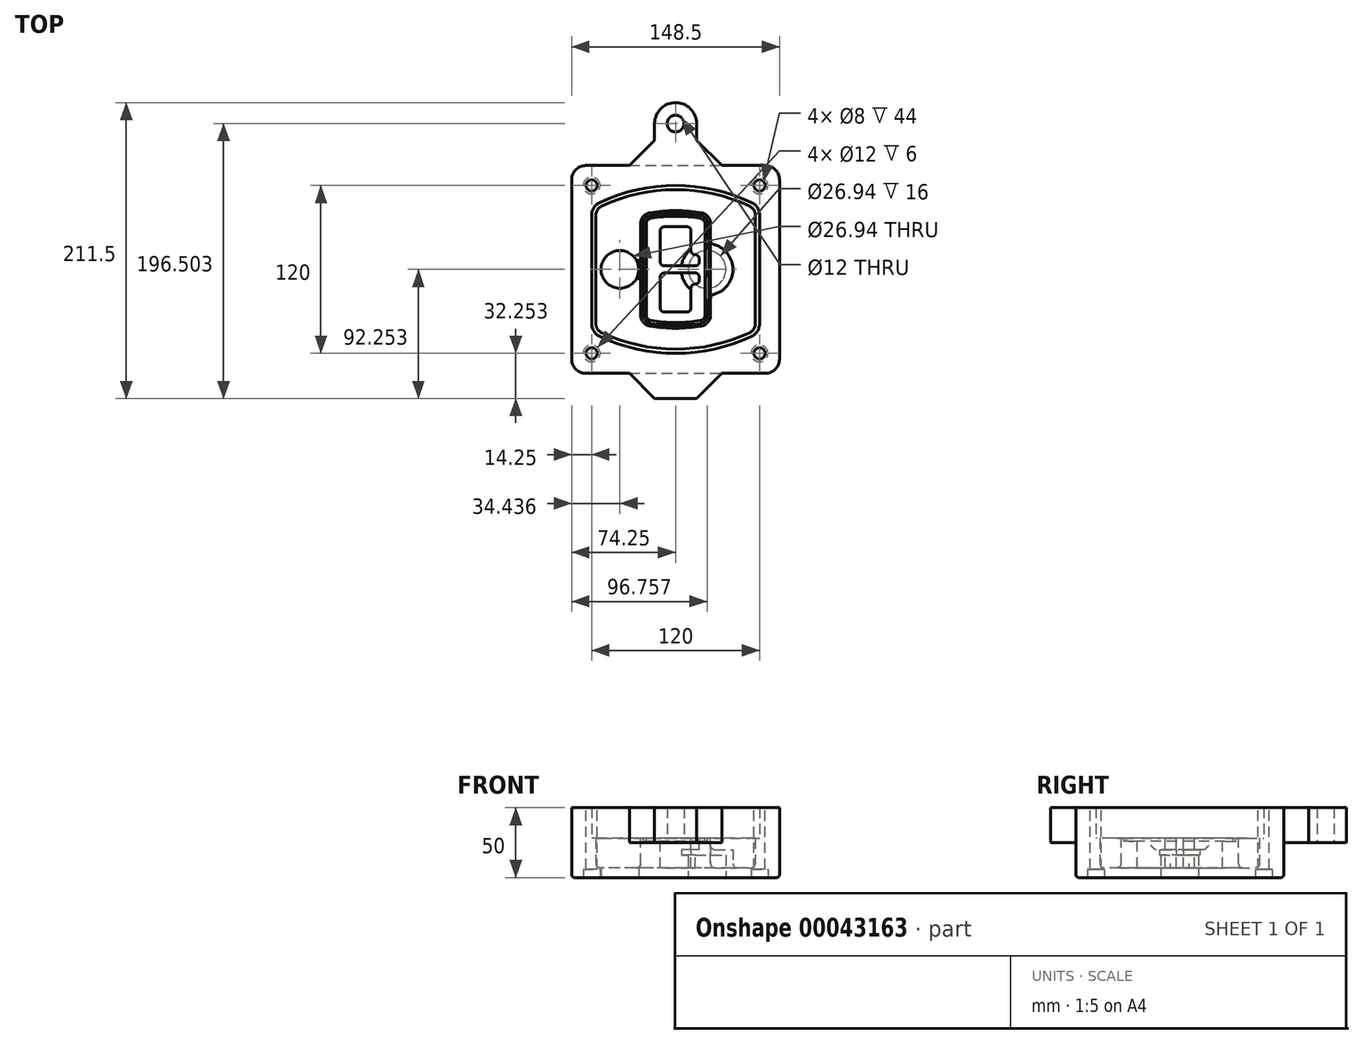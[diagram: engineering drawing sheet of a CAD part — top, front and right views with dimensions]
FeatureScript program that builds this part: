
annotation { "Feature Type Name" : "Feature", "Feature Type Description" : "" }
export const myFeature = defineFeature(function(context is Context, id is Id, definition is map)
    precondition{}
    {
        {
            var Q0;
            Q0=qCreatedBy(makeId("Top.planeOp"),FACE);
            var sketch = newSketch(context, id + "F0", { "sketchPlane" : qUnion([Q0])});
            skPoint(sketch, "E0.rect.middle", {"position": v(0, 0) * mm});
            skLineSegment(sketch, "E1.bottom", {"start": v(24.05, 28.38) * mm, "end": v(152.55, 28.38) * mm});
            skLineSegment(sketch, "E1.top", {"start": v(24.05, 176.88) * mm, "end": v(152.55, 176.88) * mm});
            skLineSegment(sketch, "E1.left", {"start": v(14.05, 38.38) * mm, "end": v(14.05, 166.88) * mm});
            skLineSegment(sketch, "E1.right", {"start": v(162.55, 38.38) * mm, "end": v(162.55, 166.88) * mm});
            skLineSegment(sketch, "E2", {"start": v(14.05, 176.88) * mm, "end": v(162.55, 28.38) * mm, "construction": true});
            skLineSegment(sketch, "E3", {"start": v(162.55, 176.88) * mm, "end": v(14.05, 28.38) * mm, "construction": true});
            skCircle(sketch, "E4", {"center": v(28.3, 162.63) * mm, "radius": 4 * mm});
            skCircle(sketch, "E5", {"center": v(148.3, 162.63) * mm, "radius": 4 * mm});
            skCircle(sketch, "E6", {"center": v(148.3, 42.63) * mm, "radius": 4 * mm});
            skCircle(sketch, "E7", {"center": v(28.3, 42.63) * mm, "radius": 4 * mm});
            skLineSegment(sketch, "E8", {"start": v(28.3, 162.63) * mm, "end": v(148.3, 162.63) * mm, "construction": true});
            skLineSegment(sketch, "E9", {"start": v(148.3, 162.63) * mm, "end": v(148.3, 42.63) * mm, "construction": true});
            skLineSegment(sketch, "E10", {"start": v(148.3, 42.63) * mm, "end": v(28.3, 42.63) * mm, "construction": true});
            skLineSegment(sketch, "E11", {"start": v(28.3, 42.63) * mm, "end": v(28.3, 162.63) * mm, "construction": true});
            skLineSegment(sketch, "E12", {"start": v(28.3, 141.46) * mm, "end": v(28.3, 63.8) * mm});
            skLineSegment(sketch, "E13", {"start": v(148.3, 141.46) * mm, "end": v(148.3, 63.8) * mm});
            skArc(sketch, "E14", {"start": v(142.56, 150.51) * mm, "mid": v(88.3, 162.63) * mm, "end": v(34.04, 150.51) * mm});
            skArc(sketch, "E15", {"start": v(34.04, 54.75) * mm, "mid": v(88.3, 42.63) * mm, "end": v(142.56, 54.75) * mm});
            skLineSegment(sketch, "E16", {"start": v(28.3, 102.63) * mm, "end": v(148.3, 102.63) * mm, "construction": true});
            skPoint(sketch, "E17.visualSharp", {"position": v(28.3, 57.63) * mm});
            skArc(sketch, "E17.filletArc", {"start": v(28.3, 63.8) * mm, "mid": v(29.86, 58.44) * mm, "end": v(34.04, 54.75) * mm});
            skPoint(sketch, "E18.visualSharp", {"position": v(28.3, 147.63) * mm});
            skArc(sketch, "E18.filletArc", {"start": v(34.04, 150.51) * mm, "mid": v(29.86, 146.82) * mm, "end": v(28.3, 141.46) * mm});
            skPoint(sketch, "E19.visualSharp", {"position": v(148.3, 147.63) * mm});
            skArc(sketch, "E19.filletArc", {"start": v(148.3, 141.46) * mm, "mid": v(146.74, 146.82) * mm, "end": v(142.56, 150.51) * mm});
            skPoint(sketch, "E20.visualSharp", {"position": v(148.3, 57.63) * mm});
            skArc(sketch, "E20.filletArc", {"start": v(142.56, 54.75) * mm, "mid": v(146.74, 58.44) * mm, "end": v(148.3, 63.8) * mm});
            skPoint(sketch, "E21.visualSharp", {"position": v(14.05, 176.88) * mm});
            skArc(sketch, "E21.filletArc", {"start": v(24.05, 176.88) * mm, "mid": v(16.98, 173.95) * mm, "end": v(14.05, 166.88) * mm});
            skPoint(sketch, "E22.visualSharp", {"position": v(162.55, 176.88) * mm});
            skArc(sketch, "E22.filletArc", {"start": v(162.55, 166.88) * mm, "mid": v(159.62, 173.95) * mm, "end": v(152.55, 176.88) * mm});
            skPoint(sketch, "E23.visualSharp", {"position": v(162.55, 28.38) * mm});
            skArc(sketch, "E23.filletArc", {"start": v(152.55, 28.38) * mm, "mid": v(159.62, 31.31) * mm, "end": v(162.55, 38.38) * mm});
            skPoint(sketch, "E24.visualSharp", {"position": v(14.05, 28.38) * mm});
            skArc(sketch, "E24.filletArc", {"start": v(14.05, 38.38) * mm, "mid": v(16.98, 31.31) * mm, "end": v(24.05, 28.38) * mm});
            skArc(sketch, "E25.0", {"start": v(145.3, 141.46) * mm, "mid": v(144.2, 145.22) * mm, "end": v(141.28, 147.8) * mm});
            skLineSegment(sketch, "E25.1", {"start": v(145.3, 141.46) * mm, "end": v(145.3, 63.8) * mm});
            skArc(sketch, "E25.2", {"start": v(141.28, 57.47) * mm, "mid": v(144.2, 60.05) * mm, "end": v(145.3, 63.8) * mm});
            skArc(sketch, "E25.3", {"start": v(35.32, 57.47) * mm, "mid": v(88.3, 45.63) * mm, "end": v(141.28, 57.47) * mm});
            skArc(sketch, "E25.4", {"start": v(31.3, 63.8) * mm, "mid": v(32.4, 60.05) * mm, "end": v(35.32, 57.47) * mm});
            skArc(sketch, "E25.5", {"start": v(141.28, 147.8) * mm, "mid": v(88.3, 159.63) * mm, "end": v(35.32, 147.8) * mm});
            skLineSegment(sketch, "E25.6", {"start": v(31.3, 141.46) * mm, "end": v(31.3, 63.8) * mm});
            skArc(sketch, "E25.7", {"start": v(35.32, 147.8) * mm, "mid": v(32.4, 145.22) * mm, "end": v(31.3, 141.46) * mm});
            skArc(sketch, "E26.0", {"start": v(32.34, 154.13) * mm, "mid": v(26.48, 148.97) * mm, "end": v(24.3, 141.46) * mm});
            skArc(sketch, "E26.1", {"start": v(144.26, 154.13) * mm, "mid": v(88.3, 166.63) * mm, "end": v(32.34, 154.13) * mm});
            skArc(sketch, "E26.2", {"start": v(152.3, 141.46) * mm, "mid": v(150.12, 148.97) * mm, "end": v(144.26, 154.13) * mm});
            skLineSegment(sketch, "E26.3", {"start": v(152.3, 141.46) * mm, "end": v(152.3, 63.8) * mm});
            skArc(sketch, "E26.4", {"start": v(144.26, 51.13) * mm, "mid": v(150.12, 56.3) * mm, "end": v(152.3, 63.8) * mm});
            skLineSegment(sketch, "E26.5", {"start": v(24.3, 141.46) * mm, "end": v(24.3, 63.8) * mm});
            skArc(sketch, "E26.6", {"start": v(32.34, 51.13) * mm, "mid": v(88.3, 38.63) * mm, "end": v(144.26, 51.13) * mm});
            skArc(sketch, "E26.7", {"start": v(24.3, 63.8) * mm, "mid": v(26.48, 56.3) * mm, "end": v(32.34, 51.13) * mm});
            skSolve(sketch);
        }
        {
            var Q0;
            Q0=makeQuery(id+"F0.imprint","IMPRINT",FACE,{"disambiguationData":[TD([[makeQuery(id+"F0.imprint","IMPRINT",EDGE,{"derivedFrom":sQuery(id+"F0.wireOp",EDGE,"E1.bottom")}),1.0]])]});
            var Q1;
            Q1=makeQuery(id+"F0.imprint","IMPRINT",FACE,{"disambiguationData":[TD([[makeQuery(id+"F0.imprint","IMPRINT",EDGE,{"derivedFrom":sQuery(id+"F0.wireOp",EDGE,"E12")}),1.0]])]});
            var Q2;
            Q2=makeQuery(id+"F0.imprint","IMPRINT",FACE,{"disambiguationData":[TD([[makeQuery(id+"F0.imprint","IMPRINT",EDGE,{"derivedFrom":sQuery(id+"F0.wireOp",EDGE,"E25.0")}),1.0]])]});
            var Q3;
            Q3=makeQuery(id+"F0.imprint","IMPRINT",FACE,{"disambiguationData":[TD([[makeQuery(id+"F0.imprint","IMPRINT",EDGE,{"derivedFrom":sQuery(id+"F0.wireOp",EDGE,"E12")}),-1.0]])]});
            extrude(context, id + "F1", {"entities" : qUnion([Q0, Q1, Q2, Q3]), "oppositeDirection" : true, "depth" : 25 * mm});
        }
        {
            var Q0;
            Q0=makeQuery(id+"F0.imprint","IMPRINT",FACE,{"disambiguationData":[TD([[makeQuery(id+"F0.imprint","IMPRINT",EDGE,{"derivedFrom":sQuery(id+"F0.wireOp",EDGE,"E12")}),1.0]])]});
            extrude(context, id + "F2", {"entities" : qUnion([Q0]), "operationType" : NewBodyOperationType.ADD, "depth" : 3 * mm});
        }
        {
            var Q0;
            Q0=makeQuery(id+"F0.imprint","IMPRINT",FACE,{"disambiguationData":[TD([[makeQuery(id+"F0.imprint","IMPRINT",EDGE,{"derivedFrom":sQuery(id+"F0.wireOp",EDGE,"E25.0")}),1.0]])]});
            extrude(context, id + "F3", {"entities" : qUnion([Q0]), "operationType" : NewBodyOperationType.REMOVE, "oppositeDirection" : true, "depth" : 18 * mm});
        }
        {
            var Q0;
            Q0=makeQuery(id+"F2.opExtrude","CAP_FACE",FACE,{"disambiguationData":[OSD([sQuery(id+"F0.wireOp",EDGE,"E12"),sQuery(id+"F0.wireOp",EDGE,"E13"),sQuery(id+"F0.wireOp",EDGE,"E14"),sQuery(id+"F0.wireOp",EDGE,"E15"),sQuery(id+"F0.wireOp",EDGE,"E17.filletArc"),sQuery(id+"F0.wireOp",EDGE,"E18.filletArc"),sQuery(id+"F0.wireOp",EDGE,"E19.filletArc"),sQuery(id+"F0.wireOp",EDGE,"E20.filletArc"),sQuery(id+"F0.wireOp",EDGE,"E25.0"),sQuery(id+"F0.wireOp",EDGE,"E25.1"),sQuery(id+"F0.wireOp",EDGE,"E25.2"),sQuery(id+"F0.wireOp",EDGE,"E25.3"),sQuery(id+"F0.wireOp",EDGE,"E25.4"),sQuery(id+"F0.wireOp",EDGE,"E25.5"),sQuery(id+"F0.wireOp",EDGE,"E25.6"),sQuery(id+"F0.wireOp",EDGE,"E25.7")])],"isStart":false});
            var sketch = newSketch(context, id + "F4", { "sketchPlane" : qUnion([Q0])});
            skArc(sketch, "E27.0", {"start": v(69.96, 62.18) * mm, "mid": v(88.3, 60.63) * mm, "end": v(106.64, 62.18) * mm});
            skArc(sketch, "E28.0", {"start": v(106.64, 143.09) * mm, "mid": v(88.3, 144.63) * mm, "end": v(69.96, 143.09) * mm});
            skLineSegment(sketch, "E29", {"start": v(63.3, 135.2) * mm, "end": v(63.3, 70.07) * mm});
            skLineSegment(sketch, "E30", {"start": v(113.3, 135.2) * mm, "end": v(113.3, 70.07) * mm});
            skLineSegment(sketch, "E31", {"start": v(63.3, 141.74) * mm, "end": v(113.3, 141.74) * mm, "construction": true});
            skLineSegment(sketch, "E32", {"start": v(63.3, 63.52) * mm, "end": v(113.3, 63.52) * mm, "construction": true});
            skPoint(sketch, "E33.visualSharp", {"position": v(63.3, 141.74) * mm});
            skArc(sketch, "E33.filletArc", {"start": v(69.96, 143.09) * mm, "mid": v(65.19, 140.36) * mm, "end": v(63.3, 135.2) * mm});
            skPoint(sketch, "E34.visualSharp", {"position": v(113.3, 141.74) * mm});
            skArc(sketch, "E34.filletArc", {"start": v(113.3, 135.2) * mm, "mid": v(111.41, 140.36) * mm, "end": v(106.64, 143.09) * mm});
            skPoint(sketch, "E35.visualSharp", {"position": v(113.3, 63.52) * mm});
            skArc(sketch, "E35.filletArc", {"start": v(106.64, 62.18) * mm, "mid": v(111.41, 64.9) * mm, "end": v(113.3, 70.07) * mm});
            skPoint(sketch, "E36.visualSharp", {"position": v(63.3, 63.52) * mm});
            skArc(sketch, "E36.filletArc", {"start": v(63.3, 70.07) * mm, "mid": v(65.19, 64.9) * mm, "end": v(69.96, 62.18) * mm});
            skArc(sketch, "E37.0", {"start": v(141.28, 147.8) * mm, "mid": v(88.3, 159.63) * mm, "end": v(35.32, 147.8) * mm});
            skArc(sketch, "E37.1", {"start": v(35.32, 147.8) * mm, "mid": v(32.4, 145.22) * mm, "end": v(31.3, 141.46) * mm});
            skLineSegment(sketch, "E37.2", {"start": v(31.3, 141.46) * mm, "end": v(31.3, 63.8) * mm});
            skArc(sketch, "E37.3", {"start": v(31.3, 63.8) * mm, "mid": v(32.4, 60.05) * mm, "end": v(35.32, 57.47) * mm});
            skArc(sketch, "E37.4", {"start": v(35.32, 57.47) * mm, "mid": v(88.3, 45.63) * mm, "end": v(141.28, 57.47) * mm});
            skArc(sketch, "E37.5", {"start": v(141.28, 57.47) * mm, "mid": v(144.2, 60.05) * mm, "end": v(145.3, 63.8) * mm});
            skLineSegment(sketch, "E37.6", {"start": v(145.3, 141.46) * mm, "end": v(145.3, 63.8) * mm});
            skArc(sketch, "E37.7", {"start": v(145.3, 141.46) * mm, "mid": v(144.2, 145.22) * mm, "end": v(141.28, 147.8) * mm});
            skLineSegment(sketch, "E38.0", {"start": v(111.3, 135.2) * mm, "end": v(111.3, 70.07) * mm});
            skArc(sketch, "E38.1", {"start": v(106.3, 64.15) * mm, "mid": v(109.88, 66.2) * mm, "end": v(111.3, 70.07) * mm});
            skArc(sketch, "E38.2", {"start": v(70.3, 64.15) * mm, "mid": v(88.3, 62.63) * mm, "end": v(106.3, 64.15) * mm});
            skArc(sketch, "E38.3", {"start": v(65.3, 70.07) * mm, "mid": v(66.72, 66.2) * mm, "end": v(70.3, 64.15) * mm});
            skLineSegment(sketch, "E38.4", {"start": v(65.3, 135.2) * mm, "end": v(65.3, 70.07) * mm});
            skArc(sketch, "E38.5", {"start": v(111.3, 135.2) * mm, "mid": v(109.88, 139.07) * mm, "end": v(106.3, 141.11) * mm});
            skArc(sketch, "E38.6", {"start": v(70.3, 141.11) * mm, "mid": v(66.72, 139.07) * mm, "end": v(65.3, 135.2) * mm});
            skArc(sketch, "E38.7", {"start": v(106.3, 141.11) * mm, "mid": v(88.3, 142.63) * mm, "end": v(70.3, 141.11) * mm});
            skArc(sketch, "E39.0", {"start": v(109.3, 135.2) * mm, "mid": v(108.36, 137.78) * mm, "end": v(105.97, 139.14) * mm});
            skLineSegment(sketch, "E39.1", {"start": v(109.3, 135.2) * mm, "end": v(109.3, 70.07) * mm});
            skArc(sketch, "E39.2", {"start": v(105.97, 66.12) * mm, "mid": v(108.36, 67.49) * mm, "end": v(109.3, 70.07) * mm});
            skArc(sketch, "E39.3", {"start": v(70.63, 66.12) * mm, "mid": v(88.3, 64.63) * mm, "end": v(105.97, 66.12) * mm});
            skArc(sketch, "E39.4", {"start": v(67.3, 70.07) * mm, "mid": v(68.24, 67.49) * mm, "end": v(70.63, 66.12) * mm});
            skArc(sketch, "E39.5", {"start": v(105.97, 139.14) * mm, "mid": v(88.3, 140.63) * mm, "end": v(70.63, 139.14) * mm});
            skLineSegment(sketch, "E39.6", {"start": v(67.3, 135.2) * mm, "end": v(67.3, 70.07) * mm});
            skArc(sketch, "E39.7", {"start": v(70.63, 139.14) * mm, "mid": v(68.24, 137.78) * mm, "end": v(67.3, 135.2) * mm});
            skLineSegment(sketch, "E40", {"start": v(63.3, 102.63) * mm, "end": v(113.3, 102.63) * mm, "construction": true});
            skLineSegment(sketch, "E41", {"start": v(77.3, 108.13) * mm, "end": v(77.3, 130.13) * mm});
            skLineSegment(sketch, "E42", {"start": v(80.3, 133.13) * mm, "end": v(96.3, 133.13) * mm});
            skLineSegment(sketch, "E43", {"start": v(99.3, 130.13) * mm, "end": v(99.3, 116.13) * mm});
            skLineSegment(sketch, "E44", {"start": v(102.3, 113.13) * mm, "end": v(102.3, 113.13) * mm});
            skLineSegment(sketch, "E45", {"start": v(105.3, 110.13) * mm, "end": v(105.3, 108.13) * mm});
            skLineSegment(sketch, "E46", {"start": v(102.3, 105.13) * mm, "end": v(80.3, 105.13) * mm});
            skPoint(sketch, "E47.visualSharp", {"position": v(77.3, 133.13) * mm});
            skArc(sketch, "E47.filletArc", {"start": v(80.3, 133.13) * mm, "mid": v(78.18, 132.25) * mm, "end": v(77.3, 130.13) * mm});
            skPoint(sketch, "E48.visualSharp", {"position": v(99.3, 133.13) * mm});
            skArc(sketch, "E48.filletArc", {"start": v(99.3, 130.13) * mm, "mid": v(98.42, 132.25) * mm, "end": v(96.3, 133.13) * mm});
            skPoint(sketch, "E49.visualSharp", {"position": v(99.3, 113.13) * mm});
            skArc(sketch, "E49.filletArc", {"start": v(99.3, 116.13) * mm, "mid": v(100.18, 114.01) * mm, "end": v(102.3, 113.13) * mm});
            skPoint(sketch, "E50.visualSharp", {"position": v(105.3, 113.13) * mm});
            skArc(sketch, "E50.filletArc", {"start": v(105.3, 110.13) * mm, "mid": v(104.42, 112.25) * mm, "end": v(102.3, 113.13) * mm});
            skPoint(sketch, "E51.visualSharp", {"position": v(105.3, 105.13) * mm});
            skArc(sketch, "E51.filletArc", {"start": v(102.3, 105.13) * mm, "mid": v(104.42, 106.01) * mm, "end": v(105.3, 108.13) * mm});
            skPoint(sketch, "E52.visualSharp", {"position": v(77.3, 105.13) * mm});
            skArc(sketch, "E52.filletArc", {"start": v(77.3, 108.13) * mm, "mid": v(78.18, 106.01) * mm, "end": v(80.3, 105.13) * mm});
            skLineSegment(sketch, "E53.0.MirrorCS", {"start": v(102.3, 100.13) * mm, "end": v(80.3, 100.13) * mm});
            skArc(sketch, "E54.0.MirrorCS", {"start": v(77.3, 97.13) * mm, "mid": v(78.18, 99.25) * mm, "end": v(80.3, 100.13) * mm});
            skLineSegment(sketch, "E55.0.MirrorCS", {"start": v(77.3, 97.13) * mm, "end": v(77.3, 75.13) * mm});
            skArc(sketch, "E56.0.MirrorCS", {"start": v(80.3, 72.13) * mm, "mid": v(78.18, 73.01) * mm, "end": v(77.3, 75.13) * mm});
            skLineSegment(sketch, "E57.0.MirrorCS", {"start": v(80.3, 72.13) * mm, "end": v(96.3, 72.13) * mm});
            skArc(sketch, "E58.0.MirrorCS", {"start": v(99.3, 75.13) * mm, "mid": v(98.42, 73.01) * mm, "end": v(96.3, 72.13) * mm});
            skLineSegment(sketch, "E59.0.MirrorCS", {"start": v(99.3, 75.13) * mm, "end": v(99.3, 89.13) * mm});
            skArc(sketch, "E60.0.MirrorCS", {"start": v(99.3, 89.13) * mm, "mid": v(100.18, 91.25) * mm, "end": v(102.3, 92.13) * mm});
            skArc(sketch, "E61.0.MirrorCS", {"start": v(105.3, 95.13) * mm, "mid": v(104.42, 93.01) * mm, "end": v(102.3, 92.13) * mm});
            skLineSegment(sketch, "E62.0.MirrorCS", {"start": v(105.3, 95.13) * mm, "end": v(105.3, 97.13) * mm});
            skArc(sketch, "E63.0.MirrorCS", {"start": v(102.3, 100.13) * mm, "mid": v(104.42, 99.25) * mm, "end": v(105.3, 97.13) * mm});
            skSolve(sketch);
        }
        {
            var Q0;
            Q0=makeQuery(id+"F4.imprint","IMPRINT",FACE,{"disambiguationData":[TD([[makeQuery(id+"F4.imprint","IMPRINT",EDGE,{"derivedFrom":sQuery(id+"F4.wireOp",EDGE,"E27.0")}),1.0]])]});
            var Q1;
            Q1=makeQuery(id+"F4.imprint","IMPRINT",FACE,{"disambiguationData":[TD([[makeQuery(id+"F4.imprint","IMPRINT",EDGE,{"derivedFrom":sQuery(id+"F4.wireOp",EDGE,"E38.0")}),-1.0]])]});
            var Q2;
            Q2=makeQuery(id+"F4.imprint","IMPRINT",FACE,{"disambiguationData":[TD([[makeQuery(id+"F4.imprint","IMPRINT",EDGE,{"derivedFrom":sQuery(id+"F4.wireOp",EDGE,"E39.0")}),1.0]])]});
            extrude(context, id + "F5", {"entities" : qUnion([Q0, Q1, Q2]), "operationType" : NewBodyOperationType.ADD, "endBound" : BoundingType.UP_TO_NEXT, "oppositeDirection" : true, "depth" : 25 * mm});
        }
        {
            var Q0;
            Q0=makeQuery(id+"F4.imprint","IMPRINT",FACE,{"disambiguationData":[TD([[makeQuery(id+"F4.imprint","IMPRINT",EDGE,{"derivedFrom":sQuery(id+"F4.wireOp",EDGE,"E38.0")}),-1.0]])]});
            extrude(context, id + "F6", {"entities" : qUnion([Q0]), "operationType" : NewBodyOperationType.REMOVE, "oppositeDirection" : true, "depth" : 2 * mm});
        }
        {
            var Q0;
            Q0=makeQuery(id+"F1.opExtrude","CAP_FACE",FACE,{"disambiguationData":[OSD([sQuery(id+"F0.wireOp",EDGE,"E1.bottom"),sQuery(id+"F0.wireOp",EDGE,"E1.top"),sQuery(id+"F0.wireOp",EDGE,"E1.left"),sQuery(id+"F0.wireOp",EDGE,"E1.right"),sQuery(id+"F0.wireOp",EDGE,"E4"),sQuery(id+"F0.wireOp",EDGE,"E5"),sQuery(id+"F0.wireOp",EDGE,"E6"),sQuery(id+"F0.wireOp",EDGE,"E7"),sQuery(id+"F0.wireOp",EDGE,"E21.filletArc"),sQuery(id+"F0.wireOp",EDGE,"E22.filletArc"),sQuery(id+"F0.wireOp",EDGE,"E23.filletArc"),sQuery(id+"F0.wireOp",EDGE,"E24.filletArc")])],"isStart":false});
            var sketch = newSketch(context, id + "F7", { "sketchPlane" : qUnion([Q0])});
            skCircle(sketch, "E64", {"center": v(110.8, -102.63) * mm, "radius": 13.47 * mm});
            skCircle(sketch, "E65", {"center": v(48.49, -102.63) * mm, "radius": 13.47 * mm});
            skLineSegment(sketch, "E66", {"start": v(162.55, -102.63) * mm, "end": v(14.05, -102.63) * mm});
            skCircle(sketch, "E67", {"center": v(110.8, -102.63) * mm, "radius": 18.47 * mm});
            skCircle(sketch, "E68", {"center": v(148.3, -162.63) * mm, "radius": 6 * mm});
            skCircle(sketch, "E69", {"center": v(28.3, -162.63) * mm, "radius": 6 * mm});
            skCircle(sketch, "E70", {"center": v(28.3, -42.63) * mm, "radius": 6 * mm});
            skCircle(sketch, "E71", {"center": v(148.3, -42.63) * mm, "radius": 6 * mm});
            skSolve(sketch);
        }
        {
            var Q0;
            {var subQ1=sQuery(id+"F7.wireOp",EDGE,"E66");var subQ4=sQuery(id+"F7.wireOp",EDGE,"E64");var subQ6=makeQuery(id+"F7.imprint","INTERSECT",VERTEX,{"disambiguationData":[OD(0.0)],"derivedFrom":[subQ4,subQ1]});Q0=makeQuery(id+"F7.imprint","IMPRINT",FACE,{"disambiguationData":[TD([[makeQuery(id+"F7.imprint","IMPRINT",EDGE,{"disambiguationData":[TD([[subQ6,-1.0]])],"derivedFrom":subQ4}),-1.0]])]});}
            var Q1;
            {var subQ0=sQuery(id+"F7.wireOp",EDGE,"E66");var subQ1=sQuery(id+"F7.wireOp",EDGE,"E64");var subQ3=makeQuery(id+"F7.imprint","INTERSECT",VERTEX,{"disambiguationData":[OD(0.0)],"derivedFrom":[subQ1,subQ0]});Q1=makeQuery(id+"F7.imprint","IMPRINT",FACE,{"disambiguationData":[TD([[makeQuery(id+"F7.imprint","IMPRINT",EDGE,{"disambiguationData":[TD([[subQ3,-1.0]])],"derivedFrom":subQ1}),1.0]])]});}
            var Q2;
            {var subQ0=sQuery(id+"F7.wireOp",EDGE,"E66");var subQ1=sQuery(id+"F7.wireOp",EDGE,"E64");var subQ3=makeQuery(id+"F7.imprint","INTERSECT",VERTEX,{"disambiguationData":[OD(0.0)],"derivedFrom":[subQ1,subQ0]});Q2=makeQuery(id+"F7.imprint","IMPRINT",FACE,{"disambiguationData":[TD([[makeQuery(id+"F7.imprint","IMPRINT",EDGE,{"disambiguationData":[TD([[subQ3,1.0]])],"derivedFrom":subQ1}),1.0]])]});}
            var Q3;
            {var subQ1=sQuery(id+"F7.wireOp",EDGE,"E66");var subQ4=sQuery(id+"F7.wireOp",EDGE,"E64");var subQ6=makeQuery(id+"F7.imprint","INTERSECT",VERTEX,{"disambiguationData":[OD(0.0)],"derivedFrom":[subQ4,subQ1]});Q3=makeQuery(id+"F7.imprint","IMPRINT",FACE,{"disambiguationData":[TD([[makeQuery(id+"F7.imprint","IMPRINT",EDGE,{"disambiguationData":[TD([[subQ6,1.0]])],"derivedFrom":subQ4}),-1.0]])]});}
            extrude(context, id + "F8", {"entities" : qUnion([Q0, Q1, Q2, Q3]), "operationType" : NewBodyOperationType.ADD, "oppositeDirection" : true, "depth" : 20 * mm});
        }
        {
            var Q0;
            {var subQ0=sQuery(id+"F7.wireOp",EDGE,"E66");var subQ1=sQuery(id+"F7.wireOp",EDGE,"E64");var subQ3=makeQuery(id+"F7.imprint","INTERSECT",VERTEX,{"disambiguationData":[OD(0.0)],"derivedFrom":[subQ1,subQ0]});Q0=makeQuery(id+"F7.imprint","IMPRINT",FACE,{"disambiguationData":[TD([[makeQuery(id+"F7.imprint","IMPRINT",EDGE,{"disambiguationData":[TD([[subQ3,-1.0]])],"derivedFrom":subQ1}),1.0]])]});}
            var Q1;
            {var subQ0=sQuery(id+"F7.wireOp",EDGE,"E66");var subQ1=sQuery(id+"F7.wireOp",EDGE,"E64");var subQ3=makeQuery(id+"F7.imprint","INTERSECT",VERTEX,{"disambiguationData":[OD(0.0)],"derivedFrom":[subQ1,subQ0]});Q1=makeQuery(id+"F7.imprint","IMPRINT",FACE,{"disambiguationData":[TD([[makeQuery(id+"F7.imprint","IMPRINT",EDGE,{"disambiguationData":[TD([[subQ3,1.0]])],"derivedFrom":subQ1}),1.0]])]});}
            extrude(context, id + "F9", {"entities" : qUnion([Q0, Q1]), "operationType" : NewBodyOperationType.REMOVE, "oppositeDirection" : true, "depth" : 16 * mm});
        }
        {
            var Q0;
            {var subQ0=sQuery(id+"F7.wireOp",EDGE,"E66");var subQ1=sQuery(id+"F7.wireOp",EDGE,"E65");var subQ3=makeQuery(id+"F7.imprint","INTERSECT",VERTEX,{"disambiguationData":[OD(0.0)],"derivedFrom":[subQ1,subQ0]});Q0=makeQuery(id+"F7.imprint","IMPRINT",FACE,{"disambiguationData":[TD([[makeQuery(id+"F7.imprint","IMPRINT",EDGE,{"disambiguationData":[TD([[subQ3,-1.0]])],"derivedFrom":subQ1}),1.0]])]});}
            var Q1;
            {var subQ0=sQuery(id+"F7.wireOp",EDGE,"E66");var subQ1=sQuery(id+"F7.wireOp",EDGE,"E65");var subQ3=makeQuery(id+"F7.imprint","INTERSECT",VERTEX,{"disambiguationData":[OD(0.0)],"derivedFrom":[subQ1,subQ0]});Q1=makeQuery(id+"F7.imprint","IMPRINT",FACE,{"disambiguationData":[TD([[makeQuery(id+"F7.imprint","IMPRINT",EDGE,{"disambiguationData":[TD([[subQ3,1.0]])],"derivedFrom":subQ1}),1.0]])]});}
            extrude(context, id + "F10", {"entities" : qUnion([Q0, Q1]), "operationType" : NewBodyOperationType.REMOVE, "oppositeDirection" : true, "depth" : 25 * mm});
        }
        {
            var Q0;
            Q0=makeQuery(id+"F7.imprint","IMPRINT",FACE,{"disambiguationData":[TD([[makeQuery(id+"F7.imprint","IMPRINT",EDGE,{"derivedFrom":sQuery(id+"F7.wireOp",EDGE,"E68")}),1.0]])]});
            var Q1;
            Q1=makeQuery(id+"F7.imprint","IMPRINT",FACE,{"disambiguationData":[TD([[makeQuery(id+"F7.imprint","IMPRINT",EDGE,{"derivedFrom":makeQuery(id+"F1.opExtrude","CAP_EDGE",EDGE,{"disambiguationData":[OSD([sQuery(id+"F0.wireOp",EDGE,"E5")])],"isStart":false})}),-1.0]])]});
            var Q2;
            Q2=makeQuery(id+"F7.imprint","IMPRINT",FACE,{"disambiguationData":[TD([[makeQuery(id+"F7.imprint","IMPRINT",EDGE,{"derivedFrom":sQuery(id+"F7.wireOp",EDGE,"E69")}),1.0]])]});
            var Q3;
            Q3=makeQuery(id+"F7.imprint","IMPRINT",FACE,{"disambiguationData":[TD([[makeQuery(id+"F7.imprint","IMPRINT",EDGE,{"derivedFrom":makeQuery(id+"F1.opExtrude","CAP_EDGE",EDGE,{"disambiguationData":[OSD([sQuery(id+"F0.wireOp",EDGE,"E4")])],"isStart":false})}),-1.0]])]});
            var Q4;
            Q4=makeQuery(id+"F7.imprint","IMPRINT",FACE,{"disambiguationData":[TD([[makeQuery(id+"F7.imprint","IMPRINT",EDGE,{"derivedFrom":sQuery(id+"F7.wireOp",EDGE,"E70")}),1.0]])]});
            var Q5;
            Q5=makeQuery(id+"F7.imprint","IMPRINT",FACE,{"disambiguationData":[TD([[makeQuery(id+"F7.imprint","IMPRINT",EDGE,{"derivedFrom":makeQuery(id+"F1.opExtrude","CAP_EDGE",EDGE,{"disambiguationData":[OSD([sQuery(id+"F0.wireOp",EDGE,"E7")])],"isStart":false})}),-1.0]])]});
            var Q6;
            Q6=makeQuery(id+"F7.imprint","IMPRINT",FACE,{"disambiguationData":[TD([[makeQuery(id+"F7.imprint","IMPRINT",EDGE,{"derivedFrom":sQuery(id+"F7.wireOp",EDGE,"E71")}),1.0]])]});
            var Q7;
            Q7=makeQuery(id+"F7.imprint","IMPRINT",FACE,{"disambiguationData":[TD([[makeQuery(id+"F7.imprint","IMPRINT",EDGE,{"derivedFrom":makeQuery(id+"F1.opExtrude","CAP_EDGE",EDGE,{"disambiguationData":[OSD([sQuery(id+"F0.wireOp",EDGE,"E6")])],"isStart":false})}),-1.0]])]});
            extrude(context, id + "F11", {"entities" : qUnion([Q0, Q1, Q2, Q3, Q4, Q5, Q6, Q7]), "operationType" : NewBodyOperationType.REMOVE, "oppositeDirection" : true, "depth" : 6 * mm});
        }
        {
            var Q0;
            Q0=makeQuery(id+"F9.boolean.opBoolean","COPY",FACE,{"derivedFrom":makeQuery(id+"F9.opExtrude","CAP_FACE",FACE,{"disambiguationData":[OSD([sQuery(id+"F7.wireOp",EDGE,"E64")])],"isStart":false})});
            var sketch = newSketch(context, id + "F12", { "sketchPlane" : qUnion([Q0])});
            skArc(sketch, "E72.0", {"start": v(99.3, -88.19) * mm, "mid": v(94.75, -93.5) * mm, "end": v(92.5, -100.13) * mm});
            skArc(sketch, "E72.1", {"start": v(92.5, -105.13) * mm, "mid": v(94.75, -111.76) * mm, "end": v(99.3, -117.08) * mm});
            skLineSegment(sketch, "E73", {"start": v(92.5, -105.13) * mm, "end": v(102.3, -105.13) * mm});
            skLineSegment(sketch, "E74.0", {"start": v(102.3, -100.13) * mm, "end": v(92.5, -100.13) * mm});
            skArc(sketch, "E74.1", {"start": v(102.3, -100.13) * mm, "mid": v(104.42, -99.25) * mm, "end": v(105.3, -97.13) * mm});
            skLineSegment(sketch, "E74.2", {"start": v(105.3, -95.13) * mm, "end": v(105.3, -97.13) * mm});
            skArc(sketch, "E74.3", {"start": v(105.3, -95.13) * mm, "mid": v(104.42, -93.01) * mm, "end": v(102.3, -92.13) * mm});
            skArc(sketch, "E74.4", {"start": v(99.3, -89.13) * mm, "mid": v(100.18, -91.25) * mm, "end": v(102.3, -92.13) * mm});
            skLineSegment(sketch, "E74.5", {"start": v(99.3, -88.19) * mm, "end": v(99.3, -89.13) * mm});
            skLineSegment(sketch, "E74.7", {"start": v(102.3, -105.13) * mm, "end": v(92.5, -105.13) * mm});
            skArc(sketch, "E74.8", {"start": v(102.3, -105.13) * mm, "mid": v(104.42, -106.01) * mm, "end": v(105.3, -108.13) * mm});
            skLineSegment(sketch, "E74.9", {"start": v(105.3, -110.13) * mm, "end": v(105.3, -108.13) * mm});
            skArc(sketch, "E74.10", {"start": v(105.3, -110.13) * mm, "mid": v(104.42, -112.25) * mm, "end": v(102.3, -113.13) * mm});
            skArc(sketch, "E74.11", {"start": v(99.3, -116.13) * mm, "mid": v(100.18, -114.01) * mm, "end": v(102.3, -113.13) * mm});
            skLineSegment(sketch, "E74.12", {"start": v(99.3, -117.08) * mm, "end": v(99.3, -116.13) * mm});
            skPoint(sketch, "E75.orphan", {"position": v(99.3, -130.13) * mm});
            skPoint(sketch, "E76.orphan", {"position": v(80.3, -105.13) * mm});
            skPoint(sketch, "E77.orphan", {"position": v(80.3, -100.13) * mm});
            skPoint(sketch, "E78.orphan", {"position": v(99.3, -75.13) * mm});
            skSolve(sketch);
        }
        {
            var Q0;
            {var subQ7=sQuery(id+"F12.wireOp",EDGE,"E72.0");var subQ14=sQuery(id+"F12.wireOp",EDGE,"E72.1");var subQ16=sQuery(id+"F12.wireOp",EDGE,"E74.1");var subQ18=sQuery(id+"F12.wireOp",EDGE,"E74.8");Q0=qUnion([makeQuery(id+"F12.imprint","IMPRINT",FACE,{"disambiguationData":[TD([[makeQuery(id+"F12.imprint","IMPRINT",EDGE,{"derivedFrom":subQ7}),1.0]])]}),makeQuery(id+"F12.imprint","IMPRINT",FACE,{"disambiguationData":[TD([[makeQuery(id+"F12.imprint","IMPRINT",EDGE,{"derivedFrom":subQ14}),1.0]])]}),makeQuery(id+"F12.imprint","IMPRINT",FACE,{"disambiguationData":[TD([[makeQuery(id+"F12.imprint","IMPRINT",EDGE,{"derivedFrom":subQ16}),1.0]])]}),makeQuery(id+"F12.imprint","IMPRINT",FACE,{"disambiguationData":[TD([[makeQuery(id+"F12.imprint","IMPRINT",EDGE,{"derivedFrom":subQ18}),-1.0]])]})]);}
            var Q1;
            Q1=makeQuery(id+"F5.boolean.opBoolean","SPLIT",FACE,{"disambiguationData":[TD([makeQuery(id+"F5.opExtrude","SWEPT_FACE",FACE,{"disambiguationData":[OSD([sQuery(id+"F4.wireOp",EDGE,"E41")])]})])],"derivedFrom":makeQuery(id+"F3.boolean.opBoolean","COPY",FACE,{"derivedFrom":makeQuery(id+"F3.opExtrude","CAP_FACE",FACE,{"disambiguationData":[OSD([sQuery(id+"F0.wireOp",EDGE,"E25.0"),sQuery(id+"F0.wireOp",EDGE,"E25.1"),sQuery(id+"F0.wireOp",EDGE,"E25.2"),sQuery(id+"F0.wireOp",EDGE,"E25.3"),sQuery(id+"F0.wireOp",EDGE,"E25.4"),sQuery(id+"F0.wireOp",EDGE,"E25.5"),sQuery(id+"F0.wireOp",EDGE,"E25.6"),sQuery(id+"F0.wireOp",EDGE,"E25.7")])],"isStart":false})})});
            extrude(context, id + "F13", {"entities" : qUnion([Q0]), "operationType" : NewBodyOperationType.REMOVE, "endBound" : BoundingType.UP_TO_SURFACE, "endBoundEntityFace" : qUnion([Q1]), "depth" : 25 * mm});
        }
        {
            var Q0;
            Q0=makeQuery(id+"F3.boolean.opBoolean","COPY",EDGE,{"derivedFrom":makeQuery(id+"F3.opExtrude","CAP_EDGE",EDGE,{"disambiguationData":[OSD([sQuery(id+"F0.wireOp",EDGE,"E25.6")])],"isStart":false})});
            var Q1;
            Q1=makeQuery(id+"F8.boolean.opBoolean","INTERSECT",EDGE,{"derivedFrom":[makeQuery(id+"F5.opExtrude","SWEPT_FACE",FACE,{"disambiguationData":[OSD([sQuery(id+"F4.wireOp",EDGE,"E30")])]}),makeQuery(id+"F8.opExtrude","CAP_FACE",FACE,{"disambiguationData":[OSD([sQuery(id+"F7.wireOp",EDGE,"E67")])],"isStart":false})]});
            var Q2;
            Q2=makeQuery(id+"F8.boolean.opBoolean","INTERSECT",EDGE,{"disambiguationData":[OD(1.0)],"derivedFrom":[makeQuery(id+"F5.opExtrude","SWEPT_FACE",FACE,{"disambiguationData":[OSD([sQuery(id+"F4.wireOp",EDGE,"E30")])]}),makeQuery(id+"F8.opExtrude","SWEPT_FACE",FACE,{"disambiguationData":[OSD([sQuery(id+"F7.wireOp",EDGE,"E67")])]})]});
            var Q3;
            {var subQ0=sQuery(id+"F4.wireOp",EDGE,"E30");Q3=makeQuery(id+"F8.boolean.opBoolean","SPLIT",EDGE,{"disambiguationData":[TD([makeQuery(id+"F5.opExtrude","SWEPT_FACE",FACE,{"disambiguationData":[OSD([sQuery(id+"F4.wireOp",EDGE,"E35.filletArc")])]})])],"derivedFrom":makeQuery(id+"F5.opExtrude","CAP_EDGE",EDGE,{"disambiguationData":[OSD([subQ0])],"isStart":false})});}
            var Q4;
            {var subQ0=sQuery(id+"F0.wireOp",EDGE,"E25.7");var subQ1=sQuery(id+"F0.wireOp",EDGE,"E25.1");var subQ2=sQuery(id+"F0.wireOp",EDGE,"E25.6");var subQ3=sQuery(id+"F0.wireOp",EDGE,"E25.5");var subQ4=sQuery(id+"F0.wireOp",EDGE,"E25.4");var subQ5=sQuery(id+"F0.wireOp",EDGE,"E25.0");var subQ6=sQuery(id+"F0.wireOp",EDGE,"E25.2");var subQ7=sQuery(id+"F0.wireOp",EDGE,"E25.3");Q4=makeQuery(id+"F8.boolean.opBoolean","INTERSECT",EDGE,{"derivedFrom":[makeQuery(id+"F5.boolean.opBoolean","SPLIT",FACE,{"disambiguationData":[TD([makeQuery(id+"F2.opExtrude","SWEPT_FACE",FACE,{"disambiguationData":[OSD([subQ5])]})])],"derivedFrom":makeQuery(id+"F3.boolean.opBoolean","COPY",FACE,{"derivedFrom":makeQuery(id+"F3.opExtrude","CAP_FACE",FACE,{"disambiguationData":[OSD([subQ5,subQ1,subQ6,subQ7,subQ4,subQ3,subQ2,subQ0])],"isStart":false})})}),makeQuery(id+"F8.opExtrude","SWEPT_FACE",FACE,{"disambiguationData":[OSD([sQuery(id+"F7.wireOp",EDGE,"E67")])]})]});}
            var Q5;
            Q5=makeQuery(id+"F8.boolean.opBoolean","INTERSECT",EDGE,{"disambiguationData":[OD(0.0)],"derivedFrom":[makeQuery(id+"F5.opExtrude","SWEPT_FACE",FACE,{"disambiguationData":[OSD([sQuery(id+"F4.wireOp",EDGE,"E30")])]}),makeQuery(id+"F8.opExtrude","SWEPT_FACE",FACE,{"disambiguationData":[OSD([sQuery(id+"F7.wireOp",EDGE,"E67")])]})]});
            fillet(context, id + "F14", {"entities" : qUnion([Q0, Q1, Q2, Q3, Q4, Q5]), "radius" : 3 * mm, "tangentPropagation" : true, "allowEdgeOverflow" : false});
        }
        {
            var Q0;
            Q0=makeQuery(id+"F1.opExtrude","CAP_EDGE",EDGE,{"disambiguationData":[OSD([sQuery(id+"F0.wireOp",EDGE,"E1.bottom")])],"isStart":false});
            fillet(context, id + "F15", {"entities" : qUnion([Q0]), "radius" : 2 * mm, "tangentPropagation" : true, "allowEdgeOverflow" : false});
        }
        {
            var Q0;
            {var subQ0=sQuery(id+"F0.wireOp",EDGE,"E1.bottom");var subQ1=sQuery(id+"F0.wireOp",EDGE,"E1.top");var subQ2=sQuery(id+"F0.wireOp",EDGE,"E1.left");var subQ3=sQuery(id+"F0.wireOp",EDGE,"E1.right");var subQ4=sQuery(id+"F0.wireOp",EDGE,"E4");var subQ5=sQuery(id+"F0.wireOp",EDGE,"E5");var subQ6=sQuery(id+"F0.wireOp",EDGE,"E6");var subQ7=sQuery(id+"F0.wireOp",EDGE,"E7");var subQ8=sQuery(id+"F0.wireOp",EDGE,"E21.filletArc");var subQ9=sQuery(id+"F0.wireOp",EDGE,"E22.filletArc");var subQ10=sQuery(id+"F0.wireOp",EDGE,"E23.filletArc");var subQ11=sQuery(id+"F0.wireOp",EDGE,"E24.filletArc");Q0=makeQuery(id+"F2.boolean.opBoolean","SPLIT",FACE,{"disambiguationData":[TD([makeQuery(id+"F1.opExtrude","SWEPT_FACE",FACE,{"disambiguationData":[OSD([subQ0])]})])],"derivedFrom":makeQuery(id+"F1.opExtrude","CAP_FACE",FACE,{"disambiguationData":[OSD([subQ0,subQ1,subQ2,subQ3,subQ4,subQ5,subQ6,subQ7,subQ8,subQ9,subQ10,subQ11])],"isStart":true})});}
            var sketch = newSketch(context, id + "F16", { "sketchPlane" : qUnion([Q0])});
            skCircle(sketch, "E79.0", {"center": v(28.3, 162.63) * mm, "radius": 4 * mm});
            skLineSegment(sketch, "E79.1", {"start": v(24.05, 176.88) * mm, "end": v(152.55, 176.88) * mm});
            skArc(sketch, "E79.2", {"start": v(24.05, 176.88) * mm, "mid": v(16.98, 173.95) * mm, "end": v(14.05, 166.88) * mm});
            skLineSegment(sketch, "E79.3", {"start": v(14.05, 38.38) * mm, "end": v(14.05, 166.88) * mm});
            skLineSegment(sketch, "E79.4", {"start": v(24.05, 28.38) * mm, "end": v(152.55, 28.38) * mm});
            skArc(sketch, "E79.5", {"start": v(14.05, 38.38) * mm, "mid": v(16.98, 31.31) * mm, "end": v(24.05, 28.38) * mm});
            skArc(sketch, "E79.6", {"start": v(152.55, 28.38) * mm, "mid": v(159.62, 31.31) * mm, "end": v(162.55, 38.38) * mm});
            skLineSegment(sketch, "E79.7", {"start": v(162.55, 38.38) * mm, "end": v(162.55, 166.88) * mm});
            skArc(sketch, "E79.8", {"start": v(162.55, 166.88) * mm, "mid": v(159.62, 173.95) * mm, "end": v(152.55, 176.88) * mm});
            skCircle(sketch, "E79.9", {"center": v(148.3, 162.63) * mm, "radius": 4 * mm});
            skArc(sketch, "E79.10", {"start": v(142.56, 150.51) * mm, "mid": v(88.3, 162.63) * mm, "end": v(34.04, 150.51) * mm});
            skArc(sketch, "E79.11", {"start": v(148.3, 141.46) * mm, "mid": v(146.74, 146.82) * mm, "end": v(142.56, 150.51) * mm});
            skLineSegment(sketch, "E79.12", {"start": v(148.3, 141.46) * mm, "end": v(148.3, 63.8) * mm});
            skArc(sketch, "E79.13", {"start": v(142.56, 54.75) * mm, "mid": v(146.74, 58.44) * mm, "end": v(148.3, 63.8) * mm});
            skArc(sketch, "E79.14", {"start": v(34.04, 54.75) * mm, "mid": v(88.3, 42.63) * mm, "end": v(142.56, 54.75) * mm});
            skArc(sketch, "E79.15", {"start": v(28.3, 63.8) * mm, "mid": v(29.86, 58.44) * mm, "end": v(34.04, 54.75) * mm});
            skLineSegment(sketch, "E79.16", {"start": v(28.3, 141.46) * mm, "end": v(28.3, 63.8) * mm});
            skPoint(sketch, "E79.17", {"position": v(34.04, 150.51) * mm});
            skArc(sketch, "E79.18", {"start": v(34.04, 150.51) * mm, "mid": v(29.86, 146.82) * mm, "end": v(28.3, 141.46) * mm});
            skCircle(sketch, "E79.19", {"center": v(148.3, 42.63) * mm, "radius": 4 * mm});
            skCircle(sketch, "E79.20", {"center": v(28.3, 42.63) * mm, "radius": 4 * mm});
            skLineSegment(sketch, "E80", {"start": v(88.3, 176.88) * mm, "end": v(88.3, 206.88) * mm, "construction": true});
            skCircle(sketch, "E81", {"center": v(88.3, 206.88) * mm, "radius": 6 * mm});
            skArc(sketch, "E82", {"start": v(103.3, 206.88) * mm, "mid": v(88.3, 221.88) * mm, "end": v(73.3, 206.88) * mm});
            skLineSegment(sketch, "E83", {"start": v(73.3, 206.88) * mm, "end": v(73.3, 194.88) * mm});
            skLineSegment(sketch, "E84", {"start": v(73.3, 194.88) * mm, "end": v(55.3, 176.88) * mm});
            skLineSegment(sketch, "E85", {"start": v(103.3, 206.88) * mm, "end": v(103.3, 194.88) * mm});
            skLineSegment(sketch, "E86", {"start": v(103.3, 194.88) * mm, "end": v(121.3, 176.88) * mm});
            skLineSegment(sketch, "E87", {"start": v(73.3, 194.88) * mm, "end": v(103.3, 194.88) * mm, "construction": true});
            skLineSegment(sketch, "E88", {"start": v(14.05, 102.63) * mm, "end": v(162.55, 102.63) * mm, "construction": true});
            skArc(sketch, "E89.MirrorCS", {"start": v(103.3, -1.62) * mm, "mid": v(88.3, -16.62) * mm, "end": v(73.3, -1.62) * mm, "construction": true});
            skCircle(sketch, "E90.MirrorC", {"center": v(88.3, -1.62) * mm, "radius": 6 * mm, "construction": true});
            skLineSegment(sketch, "E91.MirrorCS", {"start": v(103.3, -1.62) * mm, "end": v(103.3, 10.38) * mm, "construction": true});
            skLineSegment(sketch, "E92.MirrorCS", {"start": v(73.3, -1.62) * mm, "end": v(73.3, 10.38) * mm, "construction": true});
            skLineSegment(sketch, "E93.MirrorCS", {"start": v(73.3, 10.38) * mm, "end": v(55.3, 28.38) * mm, "construction": true});
            skLineSegment(sketch, "E94.MirrorCS", {"start": v(103.3, 10.38) * mm, "end": v(121.3, 28.38) * mm, "construction": true});
            skLineSegment(sketch, "E95.MirrorCS", {"start": v(88.3, 28.38) * mm, "end": v(88.3, -1.62) * mm, "construction": true});
            skLineSegment(sketch, "E96.MirrorCS", {"start": v(73.3, 10.38) * mm, "end": v(103.3, 10.38) * mm, "construction": true});
            skLineSegment(sketch, "E97.MirrorCS", {"start": v(103.3, 194.88) * mm, "end": v(121.3, 176.88) * mm, "construction": true});
            skArc(sketch, "E98.MirrorCS", {"start": v(103.3, -1.62) * mm, "mid": v(88.3, -16.62) * mm, "end": v(73.3, -1.62) * mm});
            skLineSegment(sketch, "E99.MirrorCS", {"start": v(103.3, -1.62) * mm, "end": v(103.3, 10.38) * mm});
            skLineSegment(sketch, "E100.MirrorCS", {"start": v(103.3, 10.38) * mm, "end": v(121.3, 28.38) * mm});
            skLineSegment(sketch, "E101.MirrorCS", {"start": v(73.3, 10.38) * mm, "end": v(55.3, 28.38) * mm});
            skLineSegment(sketch, "E102.MirrorCS", {"start": v(73.3, -1.62) * mm, "end": v(73.3, 10.38) * mm});
            skCircle(sketch, "E103.MirrorC", {"center": v(88.3, -1.62) * mm, "radius": 6 * mm});
            skLineSegment(sketch, "E104.MirrorCS", {"start": v(88.3, 28.38) * mm, "end": v(88.3, -1.62) * mm});
            skLineSegment(sketch, "E105.MirrorCS", {"start": v(73.3, 10.38) * mm, "end": v(103.3, 10.38) * mm});
            skSolve(sketch);
        }
        {
            var Q0;
            Q0=makeQuery(id+"F16.imprint","IMPRINT",FACE,{"disambiguationData":[TD([[makeQuery(id+"F16.imprint","IMPRINT",EDGE,{"derivedFrom":sQuery(id+"F16.wireOp",EDGE,"E81")}),-1.0]])]});
            var Q1;
            Q1=makeQuery(id+"F16.imprint","IMPRINT",FACE,{"disambiguationData":[TD([[makeQuery(id+"F16.imprint","IMPRINT",EDGE,{"derivedFrom":sQuery(id+"F16.wireOp",EDGE,"E79.0")}),-1.0]])]});
            var Q2;
            {var subQ3=sQuery(id+"F16.wireOp",EDGE,"E100.MirrorCS");Q2=makeQuery(id+"F16.imprint","IMPRINT",FACE,{"disambiguationData":[TD([[makeQuery(id+"F16.imprint","IMPRINT",EDGE,{"derivedFrom":subQ3}),1.0]])]});}
            var Q3;
            {var subQ5=sQuery(id+"F16.wireOp",EDGE,"E101.MirrorCS");Q3=makeQuery(id+"F16.imprint","IMPRINT",FACE,{"disambiguationData":[TD([[makeQuery(id+"F16.imprint","IMPRINT",EDGE,{"derivedFrom":subQ5}),-1.0]])]});}
            var Q4;
            Q4=makeQuery(id+"F16.imprint","IMPRINT",FACE,{"disambiguationData":[TD([[makeQuery(id+"F16.imprint","IMPRINT",EDGE,{"derivedFrom":sQuery(id+"F16.wireOp",EDGE,"E98.MirrorCS")}),-1.0]])]});
            extrude(context, id + "F17", {"entities" : qUnion([Q0, Q1, Q2, Q3, Q4]), "operationType" : NewBodyOperationType.ADD, "depth" : 25 * mm});
        }
    });
